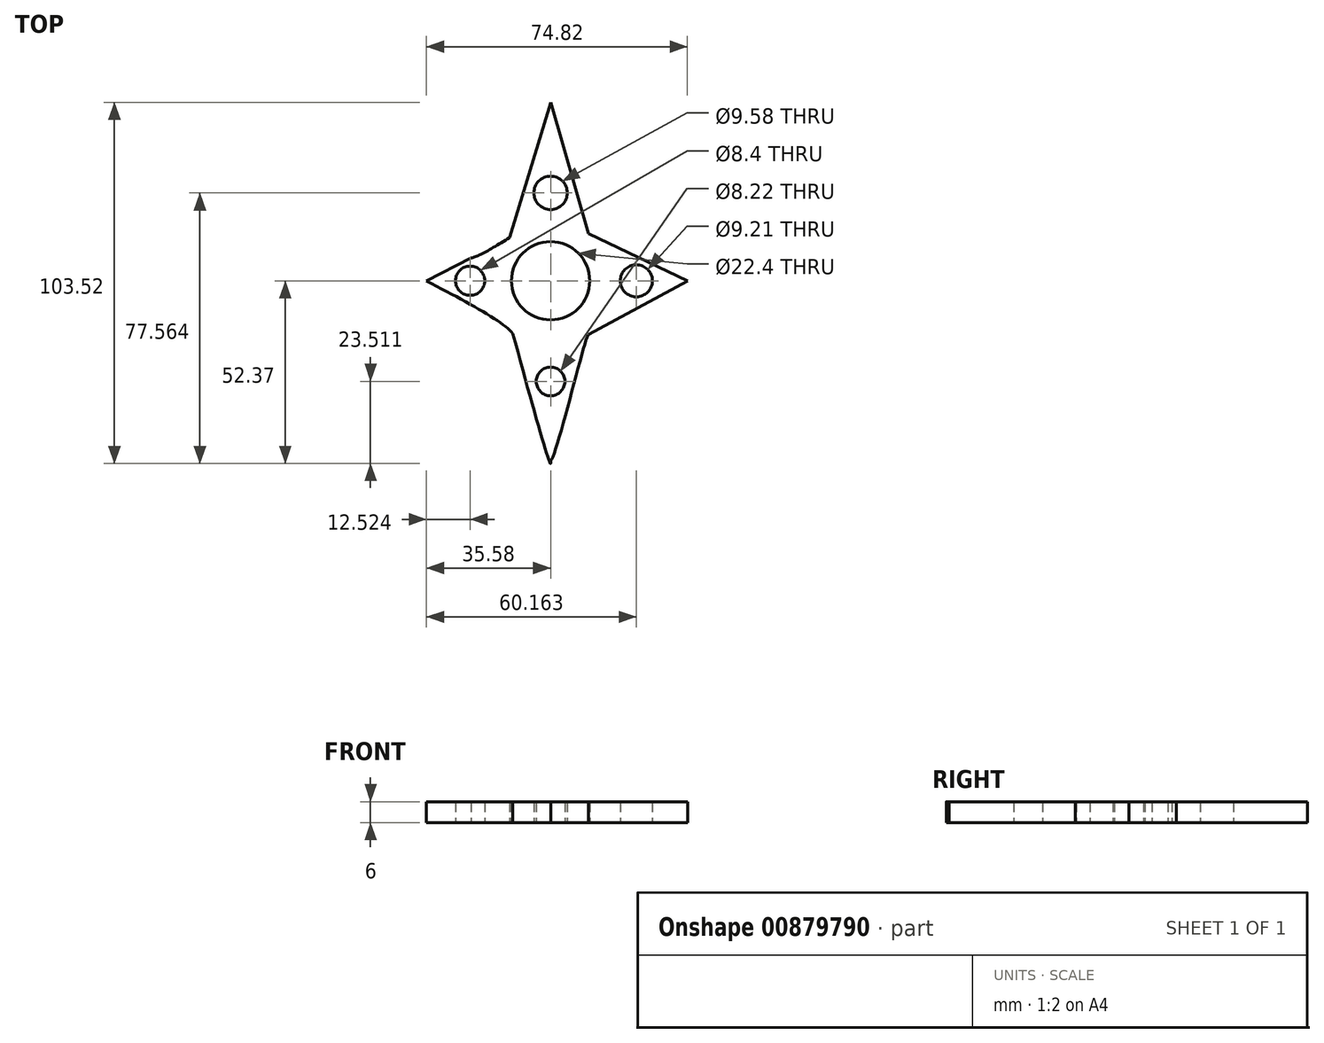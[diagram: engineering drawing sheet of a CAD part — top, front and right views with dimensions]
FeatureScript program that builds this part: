
annotation { "Feature Type Name" : "Feature", "Feature Type Description" : "" }
export const myFeature = defineFeature(function(context is Context, id is Id, definition is map)
    precondition{}
    {
        {
            var Q0;
            Q0=qCreatedBy(makeId("Top.planeOp"),FACE);
            var sketch = newSketch(context, id + "F0", { "sketchPlane" : qUnion([Q0])});
            skCircle(sketch, "E0", {"center": v(0, 0) * mm, "radius": 11.2 * mm});
            skFitSpline(sketch, "E1", {"points": [v(-11.76, 12.37) * mm, v(0, 51.15) * mm], "startDerivative": vector(11.76, 38.78) * mm, "endDerivative": vector(11.76, 38.78) * mm});
            skFitSpline(sketch, "E2", {"points": [v(0, 51.15) * mm, v(10.84, 13.59) * mm], "startDerivative": vector(10.84, -37.56) * mm, "endDerivative": vector(10.84, -37.56) * mm});
            skFitSpline(sketch, "E3", {"points": [v(-10.84, -15.12) * mm, v(0, -52.37) * mm, v(0, -50.85) * mm], "startDerivative": vector(18.41, -67.12) * mm, "endDerivative": vector(-1.08, 13.68) * mm});
            skFitSpline(sketch, "E4", {"points": [v(-0.46, -50.85) * mm, v(0.06, -51.6) * mm, v(10.84, -15.42) * mm, v(10.84, -17.25) * mm, v(10.84, -16.64) * mm], "startDerivative": vector(3.5, -14.91) * mm, "endDerivative": vector(0.44, 12.9) * mm});
            skFitSpline(sketch, "E5", {"points": [v(10.84, 13.59) * mm, v(39.24, 0) * mm], "startDerivative": vector(28.4, -13.59) * mm, "endDerivative": vector(28.4, -13.59) * mm});
            skFitSpline(sketch, "E6", {"points": [v(39.24, 0) * mm, v(10.84, -15.42) * mm], "startDerivative": vector(-28.4, -15.42) * mm, "endDerivative": vector(-28.4, -15.42) * mm});
            skFitSpline(sketch, "E7", {"points": [v(-11.76, 12.37) * mm, v(-22.75, 6.57) * mm, v(-23.97, 6.87) * mm], "startDerivative": vector(-18.07, -11.03) * mm, "endDerivative": vector(-3.92, 2.34) * mm});
            skFitSpline(sketch, "E8", {"points": [v(-22.75, 6.57) * mm, v(-35.58, 0) * mm], "startDerivative": vector(-12.83, -6.57) * mm, "endDerivative": vector(-12.83, -6.57) * mm});
            skFitSpline(sketch, "E9", {"points": [v(-35.58, 0) * mm, v(-10.84, -15.12) * mm, v(-10.12, -17.75) * mm], "startDerivative": vector(43.5, -23.03) * mm, "endDerivative": vector(-0.32, -10.2) * mm});
            skCircle(sketch, "E10", {"center": v(0, 25.2) * mm, "radius": 4.8 * mm});
            skCircle(sketch, "E11", {"center": v(-23.06, 0) * mm, "radius": 4.2 * mm});
            skCircle(sketch, "E12", {"center": v(0, -28.86) * mm, "radius": 4.11 * mm});
            skCircle(sketch, "E13", {"center": v(24.58, 0) * mm, "radius": 4.6 * mm});
            skSolve(sketch);
        }
        {
            var Q0;
            Q0 = qSketchRegion(id + "F0", true);
            extrude(context, id + "F1", {"entities" : qUnion([Q0]), "depth" : 6 * mm, "offsetDistance" : 25 * mm});
        }
    });
